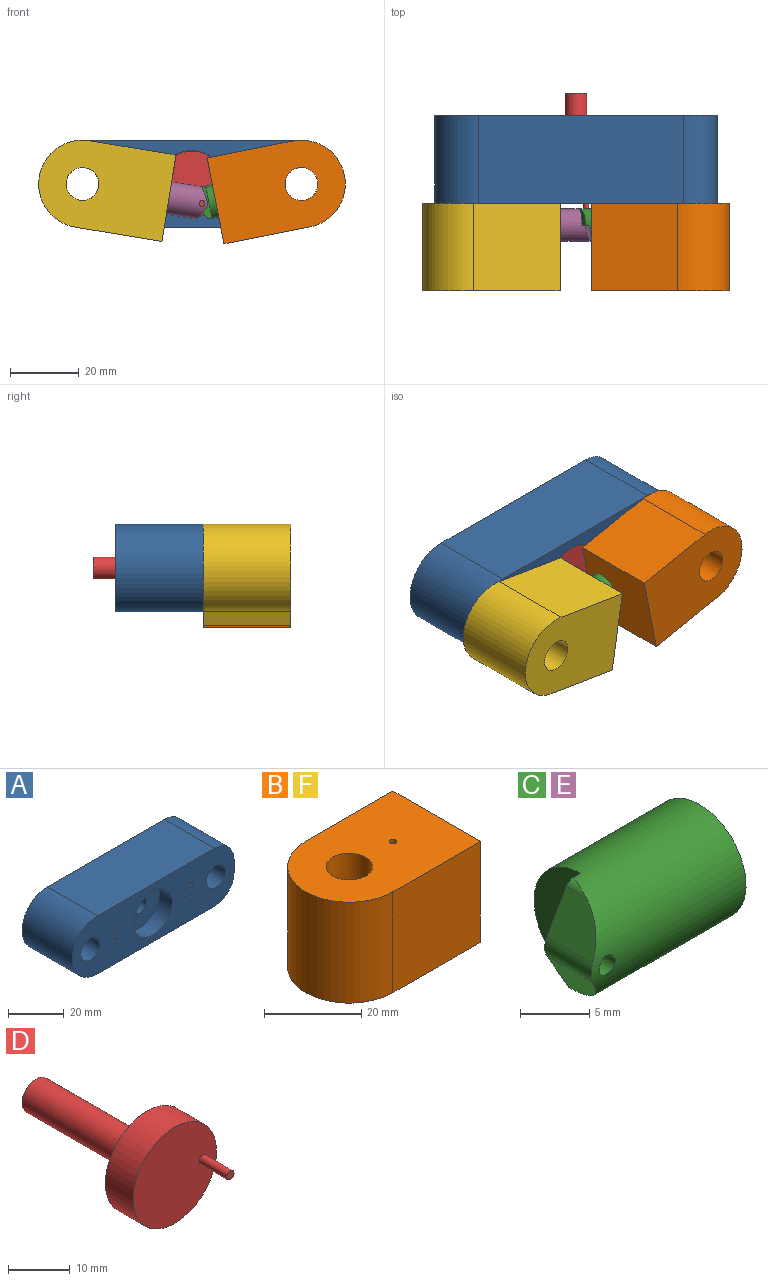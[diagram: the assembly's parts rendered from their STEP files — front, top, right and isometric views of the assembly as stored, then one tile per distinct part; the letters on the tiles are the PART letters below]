
ASSEMBLY  parts=6 mates=7
PART A: 17 faces, bbox 81.8x25.4x25.4 mm
  f0: plane 59.25x25.4mm, normal (0,0,-1), area 1504.8mm2, adj f1,f5,f13,f14
  f1: cylinder r=9.84mm len=25.4mm, axis (0,-1,0), area 392.7mm2, adj f0,f2,f13,f14
  f2: plane 25.4x5.72mm, normal (1,0,0), area 145.2mm2, adj f1,f3,f13,f14
  f3: cylinder r=9.84mm len=25.4mm, axis (0,-1,0), area 392.7mm2, adj f2,f4,f13,f14
  f4: plane 59.25x25.4mm, normal (0,0,1), area 1504.8mm2, adj f3,f5,f13,f14
  f5: cylinder r=12.7mm len=25.4mm, axis (0,-1,0), area 1013.4mm2, adj f0,f4,f13,f14
  f6: cylinder r=4.76mm len=25.4mm, axis (0,-1,0), area 760.1mm2, adj f13,f14
  f7: cylinder r=0.8mm len=25.4mm, axis (0,-1,0), area 127.7mm2, adj f13,f14
  f8: cylinder r=0.8mm len=25.4mm, axis (0,-1,0), area 127.7mm2, adj f13,f14
  f9: cylinder r=0.8mm len=25.4mm, axis (0,-1,0), area 127.7mm2, adj f13,f14
  f10: cylinder r=4.76mm len=25.4mm, axis (0,-1,0), area 760.1mm2, adj f13,f14
  f11: cylinder r=0.8mm len=25.4mm, axis (0,-1,0), area 127.7mm2, adj f13,f14
  f12: cylinder r=3.17mm len=18.92mm, axis (0,-1,0), area 377.5mm2, adj f13,f16
  f13: plane 81.79x25.4mm, normal (0,1,0), area 1784.4mm2, adj f0,f1,f2,f3,f4,f5,f6,f7
  f14: plane 81.79x25.4mm, normal (0,-1,0), area 1523.4mm2, adj f0,f1,f2,f3,f4,f5,f6,f7
  f15: cylinder r=9.65mm len=19.3mm, axis (0,-1,0), area 392.8mm2, adj f14,f16
  f16: plane 19.3x19.3mm, normal (0,-1,0), area 261mm2, adj f12,f15
PART B: 11 faces, bbox 38.1x25.4x25.4 mm
  f0: plane 25.4x25.4mm, normal (0,1,0), area 645.2mm2, adj f1,f3,f5,f6
  f1: cylinder r=12.7mm len=25.4mm, axis (0,0,1), area 1013.4mm2, adj f0,f2,f5,f6
  f2: plane 25.4x25.4mm, normal (0,-1,0), area 645.2mm2, adj f1,f3,f5,f6
  f3: plane 25.4x25.4mm, normal (1,0,0), area 557.9mm2, adj f0,f2,f5,f6,f10
  f4: cylinder r=4.76mm len=25.4mm, axis (0,0,1), area 760.1mm2, adj f5,f6
  f5: plane 38.1x25.4mm, normal (0,0,-1), area 827.3mm2, adj f0,f1,f2,f3,f4
  f6: plane 38.1x25.4mm, normal (0,0,1), area 825.3mm2, adj f0,f1,f2,f3,f4,f7
  f7: cylinder r=0.79mm len=1.65mm, axis (0,0,1), area 8.1mm2, adj f6,f8
  f8: cylinder r=4.76mm len=14.73mm, axis (1,0,0), area 438.8mm2, adj f7,f9,f10
  f9: plane 9.53x9.53mm, normal (1,0,0), area 71.3mm2, adj f8
  f10: cone r=4.76mm half-angle=45deg, axis (1,0,0), area 22.6mm2, adj f3,f8
PART C: 9 faces, bbox 15.9x9.5x9.5 mm
  f0: cylinder r=4.76mm len=15.88mm, axis (-1,0,0), area 394.8mm2, adj f1,f2,f3,f4,f5,f6,f7,f8
  f1: plane 9.53x3.68mm, normal (0,1,0), area 22.1mm2, adj f0,f3,f4,f5,f6,f7,f8
  f2: plane 9.53x9.53mm, normal (1,0,0), area 71.3mm2, adj f0
  f3: plane 9.53x4.76mm, normal (-1,0,0), area 35.6mm2, adj f0,f1
  f4: cylinder r=0.83mm len=4.69mm, axis (0,1,0), area 24.3mm2, adj f0,f1
  f5: plane 4.69x3.94mm, normal (-0.87,0,-0.5), area 16.1mm2, adj f0,f1,f6
  f6: cylinder r=1.65mm len=4.69mm, axis (0,1,0), area 8.1mm2, adj f0,f1,f5,f8
  f7: cylinder r=0.89mm len=2.01mm, axis (0,1,0), area 0.9mm2, adj f0,f1,f8
  f8: plane 4.69x3.49mm, normal (-0.87,0,0.5), area 15.4mm2, adj f0,f1,f6,f7
PART D: 7 faces, bbox 19.1x38.1x19.1 mm
  f0: cylinder r=3.17mm len=25.4mm, axis (0,-1,0), area 506.7mm2, adj f1,f4
  f1: plane 6.35x6.35mm, normal (0,1,0), area 31.7mm2, adj f0
  f2: cylinder r=9.53mm len=19.05mm, axis (0,1,0), area 380mm2, adj f3,f4
  f3: plane 19.05x19.05mm, normal (0,-1,0), area 282.9mm2, adj f2,f5
  f4: plane 19.05x19.05mm, normal (0,1,0), area 253.4mm2, adj f0,f2
  f5: cylinder r=0.83mm len=6.35mm, axis (0,1,0), area 32.9mm2, adj f3,f6
  f6: plane 1.65x1.65mm, normal (0,-1,0), area 2.1mm2, adj f5
PART E: same geometry as C
PART F: same geometry as B
PLACE A t=(-16.09,26.7,49.79)mm fixed
PLACE B rot(axis=(-0.07,0.71,0.71),172.2deg) t=(-33.16,26.7,-7.16)mm
PLACE C rot(axis=(-1,0,-0.1),180deg) t=(-19.02,59.04,65.25)mm
PLACE D rot(axis=(0,1,0),63deg) t=(-43.24,33.18,1.66)mm
PLACE E rot(axis=(0,-1,0),170.7deg) t=(-8.05,-18.34,65.42)mm
PLACE F rot(axis=(-0.99,0.08,0.08),90.4deg) t=(17.75,26.7,86.19)mm
MATE revolute B.f1 <-> A.f10  axis (0,1,0) through (15.66,26.7,49.79)mm
MATE slider E.f0 <-> F.f10  axis (0.99,0,-0.16) through (-27.24,20.35,46.42)mm
MATE slider B.f8 <-> C.f0  axis (-0.98,0,-0.19) through (-8.76,20.35,45)mm
MATE cylindrical C.f4 <-> D.f5  axis (0,-1,0) through (-13.2,20.35,44.13)mm
MATE cylindrical D.f5 <-> E.f4  axis (0,-1,0) through (-13.2,20.48,44.13)mm
MATE revolute A.f6 <-> F.f1  axis (0,-1,0) through (-47.84,26.7,49.79)mm
MATE revolute A.f12 <-> D.f0  axis (0,-1,0) through (-16.09,33.18,49.79)mm
